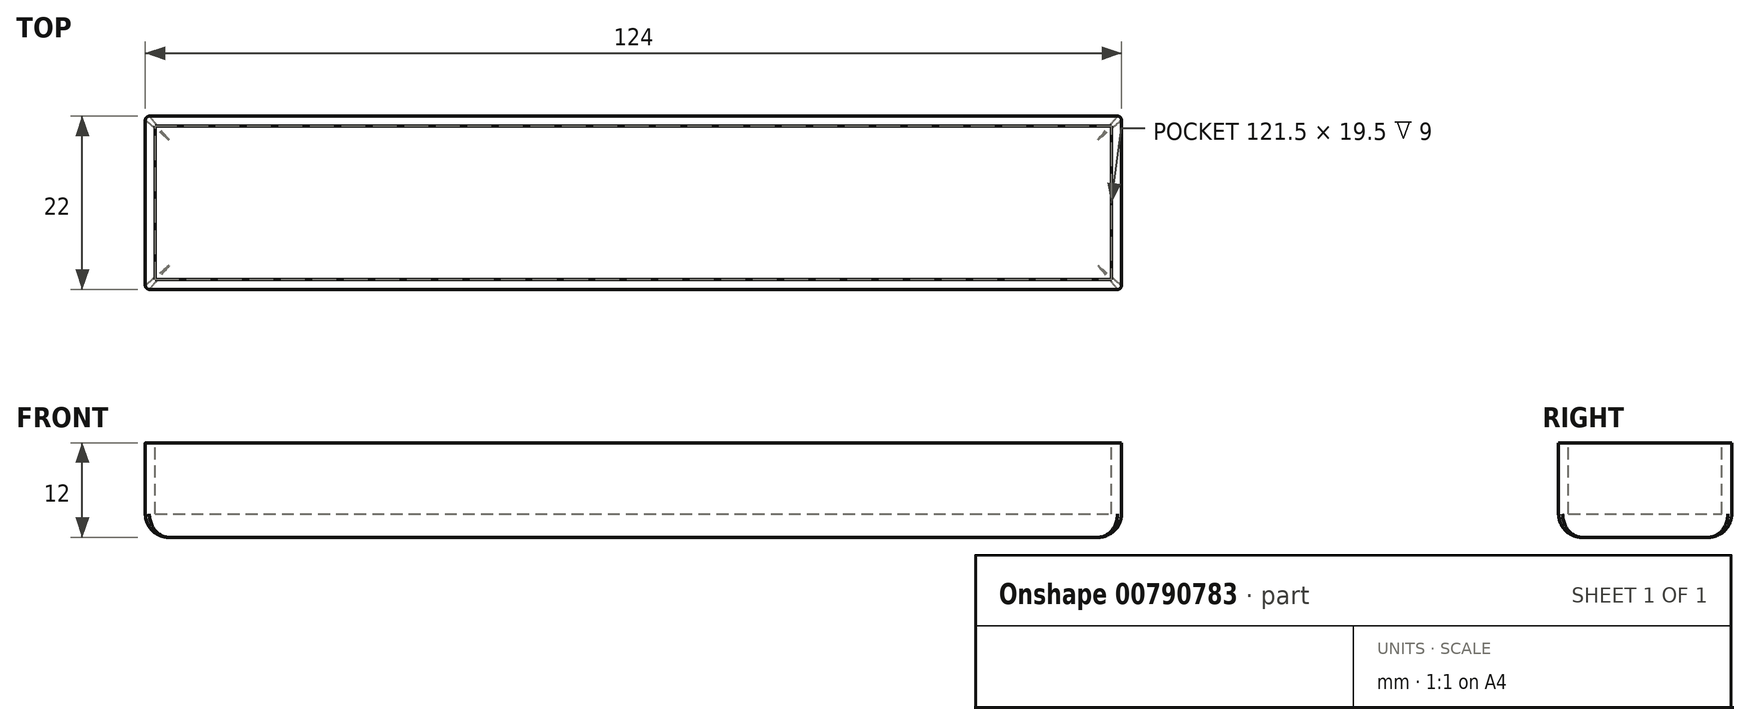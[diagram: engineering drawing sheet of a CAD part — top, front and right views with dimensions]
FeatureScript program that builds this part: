
annotation { "Feature Type Name" : "Feature", "Feature Type Description" : "" }
export const myFeature = defineFeature(function(context is Context, id is Id, definition is map)
    precondition{}
    {
        {
            var Q0;
            Q0=qCreatedBy(makeId("Top.planeOp"),FACE);
            var sketch = newSketch(context, id + "F0", { "sketchPlane" : qUnion([Q0])});
            skLineSegment(sketch, "E0.bottom", {"start": v(62, -11) * mm, "end": v(-62, -11) * mm});
            skLineSegment(sketch, "E0.top", {"start": v(62, 11) * mm, "end": v(-62, 11) * mm});
            skLineSegment(sketch, "E0.left", {"start": v(62, -11) * mm, "end": v(62, 11) * mm});
            skLineSegment(sketch, "E0.right", {"start": v(-62, -11) * mm, "end": v(-62, 11) * mm});
            skPoint(sketch, "E0.middle", {"position": v(0, 0) * mm});
            skSolve(sketch);
        }
        {
            var Q0;
            Q0 = qSketchRegion(id + "F0", true);
            extrude(context, id + "F1", {"entities" : qUnion([Q0]), "depth" : 12 * mm, "offsetDistance" : 25 * mm});
        }
        {
            var Q0;
            Q0 = qSketchRegion(id + "F0", true);
            extrude(context, id + "F2", {"entities" : qUnion([Q0]), "operationType" : NewBodyOperationType.ADD, "depth" : 11 * mm, "offsetDistance" : 25 * mm});
        }
        {
            var Q0;
            Q0=makeQuery(id+"F1.opExtrude","CAP_EDGE",EDGE,{"disambiguationData":[OSD([sQuery(id+"F0.wireOp",EDGE,"E0.bottom")])],"isStart":true});
            var Q1;
            Q1=makeQuery(id+"F1.opExtrude","CAP_EDGE",EDGE,{"disambiguationData":[OSD([sQuery(id+"F0.wireOp",EDGE,"E0.right")])],"isStart":true});
            var Q2;
            Q2=makeQuery(id+"F1.opExtrude","CAP_EDGE",EDGE,{"disambiguationData":[OSD([sQuery(id+"F0.wireOp",EDGE,"E0.top")])],"isStart":true});
            var Q3;
            Q3=makeQuery(id+"F1.opExtrude","CAP_EDGE",EDGE,{"disambiguationData":[OSD([sQuery(id+"F0.wireOp",EDGE,"E0.left")])],"isStart":true});
            fillet(context, id + "F3", {"entities" : qUnion([Q0, Q1, Q2, Q3]), "radius" : 3 * mm, "tangentPropagation" : true, "allowEdgeOverflow" : false});
        }
        {
            var Q0;
            Q0=makeQuery(id+"F1.opExtrude","CAP_FACE",FACE,{"disambiguationData":[OSD([sQuery(id+"F0.wireOp",EDGE,"E0.bottom"),sQuery(id+"F0.wireOp",EDGE,"E0.top"),sQuery(id+"F0.wireOp",EDGE,"E0.left"),sQuery(id+"F0.wireOp",EDGE,"E0.right")])],"isStart":false});
            var sketch = newSketch(context, id + "F4", { "sketchPlane" : qUnion([Q0])});
            skLineSegment(sketch, "E1.bottom", {"start": v(-60.75, -9.75) * mm, "end": v(60.75, -9.75) * mm});
            skLineSegment(sketch, "E1.top", {"start": v(-60.75, 9.75) * mm, "end": v(60.75, 9.75) * mm});
            skLineSegment(sketch, "E1.left", {"start": v(-60.75, -9.75) * mm, "end": v(-60.75, 9.75) * mm});
            skLineSegment(sketch, "E1.right", {"start": v(60.75, -9.75) * mm, "end": v(60.75, 9.75) * mm});
            skPoint(sketch, "E1.middle", {"position": v(0, 0) * mm});
            skSolve(sketch);
        }
        {
            var Q0;
            Q0 = qSketchRegion(id + "F4", true);
            extrude(context, id + "F5", {"entities" : qUnion([Q0]), "operationType" : NewBodyOperationType.REMOVE, "oppositeDirection" : true, "depth" : 9 * mm, "offsetDistance" : 25 * mm});
        }
        {
            var Q0;
            Q0=makeQuery(id+"F1.opExtrude","SWEPT_EDGE",EDGE,{"disambiguationData":[OSD([sQuery(id+"F0.wireOp",EDGE,"E0.top"),sQuery(id+"F0.wireOp",EDGE,"E0.right")])]});
            var Q1;
            Q1=makeQuery(id+"F1.opExtrude","SWEPT_EDGE",EDGE,{"disambiguationData":[OSD([sQuery(id+"F0.wireOp",EDGE,"E0.bottom"),sQuery(id+"F0.wireOp",EDGE,"E0.right")])]});
            var Q2;
            Q2=makeQuery(id+"F1.opExtrude","SWEPT_EDGE",EDGE,{"disambiguationData":[OSD([sQuery(id+"F0.wireOp",EDGE,"E0.top"),sQuery(id+"F0.wireOp",EDGE,"E0.left")])]});
            var Q3;
            Q3=makeQuery(id+"F1.opExtrude","SWEPT_EDGE",EDGE,{"disambiguationData":[OSD([sQuery(id+"F0.wireOp",EDGE,"E0.bottom"),sQuery(id+"F0.wireOp",EDGE,"E0.left")])]});
            fillet(context, id + "F6", {"entities" : qUnion([Q0, Q1, Q2, Q3]), "radius" : .5 * mm, "tangentPropagation" : true, "allowEdgeOverflow" : false});
        }
    });
